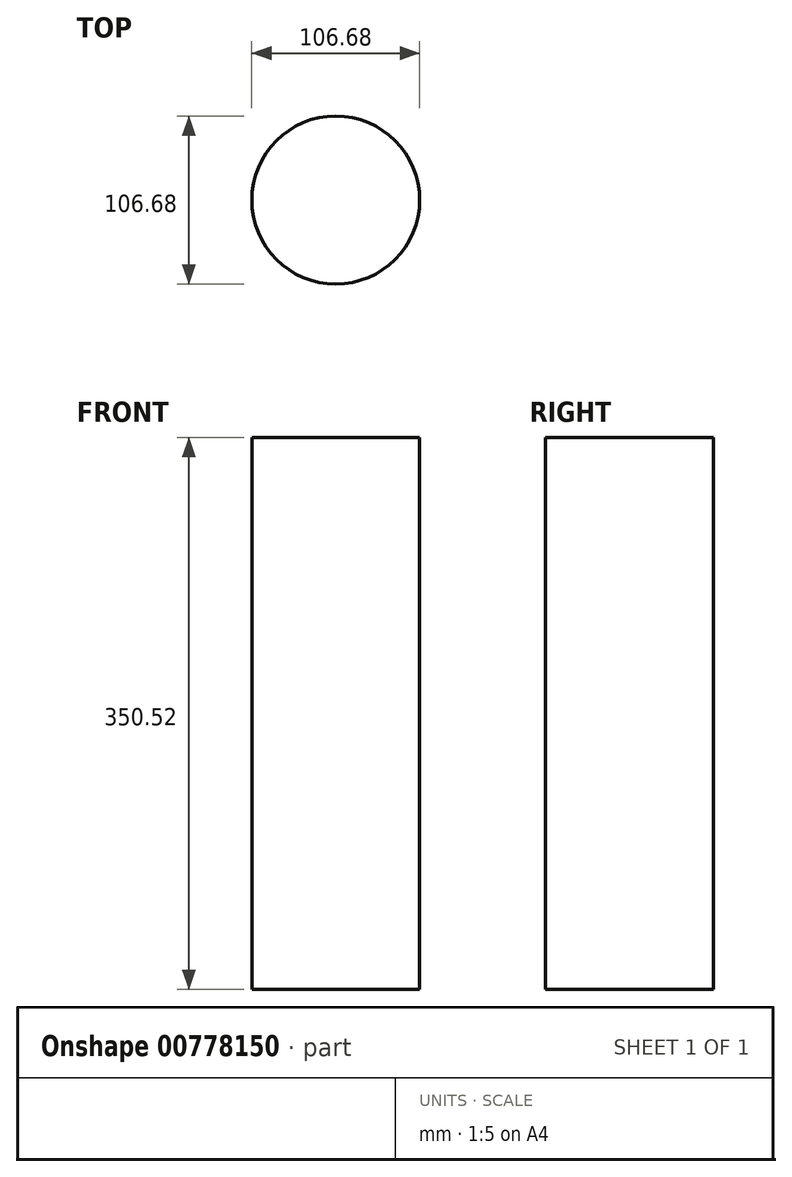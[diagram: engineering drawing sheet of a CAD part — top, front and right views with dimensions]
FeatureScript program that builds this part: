
annotation { "Feature Type Name" : "Feature", "Feature Type Description" : "" }
export const myFeature = defineFeature(function(context is Context, id is Id, definition is map)
    precondition{}
    {
        {
            var Q0;
            Q0=qCreatedBy(makeId("Top.planeOp"),FACE);
            var sketch = newSketch(context, id + "F0", { "sketchPlane" : qUnion([Q0])});
            skCircle(sketch, "E0", {"center": v(0, 0) * mm, "radius": 53.34 * mm});
            skSolve(sketch);
        }
        {
            var Q0;
            Q0 = qSketchRegion(id + "F0", true);
            extrude(context, id + "F1", {"entities" : qUnion([Q0]), "depth" : 350.52 * mm, "offsetDistance" : 25.4 * mm});
        }
    });
